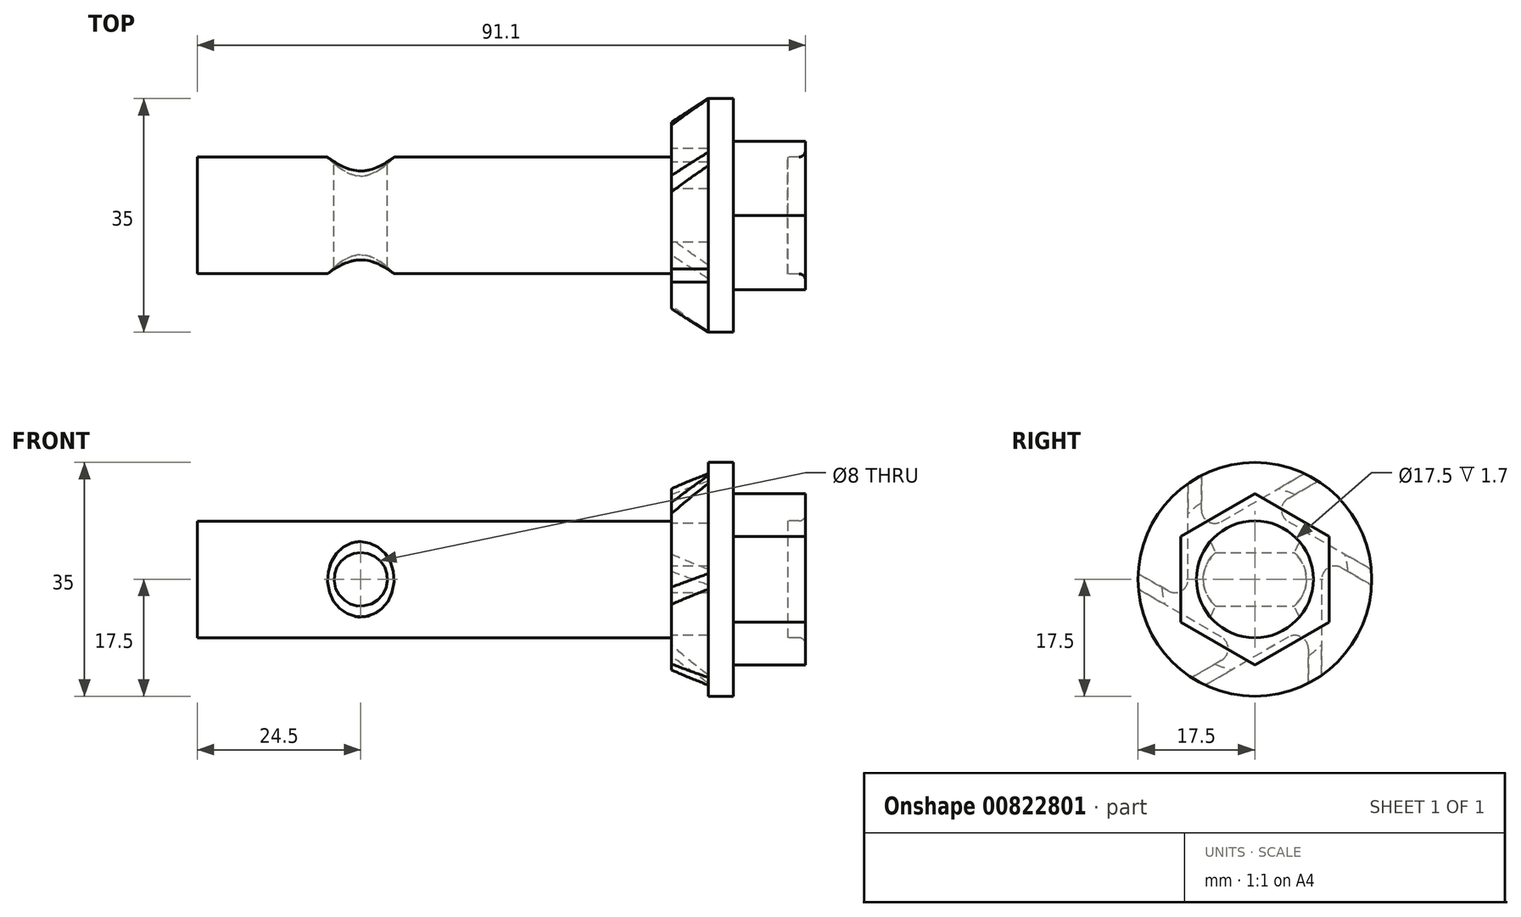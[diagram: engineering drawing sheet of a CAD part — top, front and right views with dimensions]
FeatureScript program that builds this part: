
annotation { "Feature Type Name" : "Feature", "Feature Type Description" : "" }
export const myFeature = defineFeature(function(context is Context, id is Id, definition is map)
    precondition{}
    {
        {
            var Q0;
            Q0=qCreatedBy(makeId("Front.planeOp"),FACE);
            var sketch = newSketch(context, id + "F0", { "sketchPlane" : qUnion([Q0])});
            skLineSegment(sketch, "E0", {"start": v(0, 0) * mm, "end": v(0, 8.73) * mm, "construction": true});
            skLineSegment(sketch, "E1", {"start": v(0, 8.73) * mm, "end": v(-71, 8.73) * mm});
            skLineSegment(sketch, "E2", {"start": v(-71, 8.73) * mm, "end": v(-71, 0) * mm});
            skLineSegment(sketch, "E3", {"start": v(-71, 0) * mm, "end": v(0, 0) * mm});
            skLineSegment(sketch, "E4", {"start": v(0, 8.73) * mm, "end": v(0, 14) * mm});
            skLineSegment(sketch, "E5", {"start": v(5.55, 17.5) * mm, "end": v(9.3, 17.5) * mm});
            skLineSegment(sketch, "E6", {"start": v(9.3, 17.5) * mm, "end": v(9.3, 14) * mm});
            skLineSegment(sketch, "E7", {"start": v(9.3, 14) * mm, "end": v(20.1, 14) * mm});
            skLineSegment(sketch, "E8", {"start": v(20.1, 14) * mm, "end": v(20.1, 8.75) * mm});
            skLineSegment(sketch, "E9", {"start": v(17.4, 0) * mm, "end": v(0, 0) * mm});
            skLineSegment(sketch, "E10", {"start": v(17.4, 0) * mm, "end": v(17.4, 8.75) * mm});
            skLineSegment(sketch, "E11", {"start": v(17.4, 8.75) * mm, "end": v(20.1, 8.75) * mm});
            skPoint(sketch, "E12.orphan", {"position": v(20.1, 0) * mm});
            skLineSegment(sketch, "E13", {"start": v(5.55, 17.5) * mm, "end": v(0, 14) * mm});
            skSolve(sketch);
        }
        {
            var Q0;
            Q0=qSketchRegion(id+"F0",true);
            var Q1;
            Q1=sQuery(id+"F0.wireOp",EDGE,"E3");
            revolve(context, id + "F1", {"surfaceOperationType" : NewSurfaceOperationType.NEW, "entities" : qUnion([Q0]), "axis" : qUnion([Q1]), "revolveType" : RevolveType.FULL});
        }
        {
            var Q0;
            Q0=makeQuery(id+"F1.opRevolve","SWEPT_FACE",FACE,{"disambiguationData":[OSD([sQuery(id+"F0.wireOp",EDGE,"E8")])]});
            var sketch = newSketch(context, id + "F2", { "sketchPlane" : qUnion([Q0])});
            skCircle(sketch, "E14.cCircle", {"center": v(0, 0) * mm, "radius": 11.11 * mm, "construction": true});
            skLineSegment(sketch, "E14.0", {"start": v(-11.11, -6.42) * mm, "end": v(-11.11, 6.42) * mm});
            skLineSegment(sketch, "E14.1", {"start": v(-11.11, 6.42) * mm, "end": v(0, 12.83) * mm});
            skLineSegment(sketch, "E14.2", {"start": v(0, 12.83) * mm, "end": v(11.11, 6.42) * mm});
            skLineSegment(sketch, "E14.3", {"start": v(11.11, 6.42) * mm, "end": v(11.11, -6.42) * mm});
            skLineSegment(sketch, "E14.4", {"start": v(11.11, -6.42) * mm, "end": v(0, -12.83) * mm});
            skLineSegment(sketch, "E14.5", {"start": v(0, -12.83) * mm, "end": v(-11.11, -6.42) * mm});
            skPoint(sketch, "E14.0.midPoint", {"position": v(-11.11, 0) * mm});
            skCircle(sketch, "E15", {"center": v(0, 0) * mm, "radius": 15.48 * mm});
            skSolve(sketch);
        }
        {
            var Q0;
            Q0=qSketchRegion(id+"F2",true);
            var Q1;
            Q1=makeQuery(id+"F1.opRevolve","SWEPT_FACE",FACE,{"disambiguationData":[OSD([sQuery(id+"F0.wireOp",EDGE,"E6")])]});
            extrude(context, id + "F3", {"entities" : qUnion([Q0]), "operationType" : NewBodyOperationType.REMOVE, "endBound" : BoundingType.UP_TO_SURFACE, "oppositeDirection" : true, "depth" : 25 * mm, "endBoundEntityFace" : qUnion([Q1]), "offsetDistance" : 25 * mm});
        }
        {
            var Q0;
            Q0=makeQuery(id+"F1.opRevolve","SWEPT_EDGE",EDGE,{"disambiguationData":[OSD([sQuery(id+"F0.wireOp",EDGE,"E8"),sQuery(id+"F0.wireOp",EDGE,"E11")])]});
            fillet(context, id + "F4", {"entities" : qUnion([Q0]), "radius" : 1 * mm, "tangentPropagation" : true, "allowEdgeOverflow" : false});
        }
        {
            var Q0;
            Q0=makeQuery(id+"F1.opRevolve","SWEPT_FACE",FACE,{"disambiguationData":[OSD([sQuery(id+"F0.wireOp",EDGE,"E4")])]});
            var sketch = newSketch(context, id + "F5", { "sketchPlane" : qUnion([Q0])});
            skCircle(sketch, "E16.0", {"center": v(0, 0) * mm, "radius": 17.5 * mm, "construction": true});
            skLineSegment(sketch, "E17.1.0", {"start": v(-0.3, -17.5) * mm, "end": v(-0.3, -17.5) * mm});
            skLineSegment(sketch, "E18", {"start": v(17.5, 0) * mm, "end": v(14, 0) * mm, "construction": true});
            skLineSegment(sketch, "E19", {"start": v(14, 0) * mm, "end": v(10, 0) * mm, "construction": true});
            skArc(sketch, "E20", {"start": v(10, 0) * mm, "mid": v(11, -1.73) * mm, "end": v(13, -1.73) * mm});
            skLineSegment(sketch, "E21", {"start": v(10, 0) * mm, "end": v(10, 18.81) * mm});
            skLineSegment(sketch, "E22", {"start": v(13, -1.73) * mm, "end": v(23.88, 4.55) * mm});
            skLineSegment(sketch, "E23", {"start": v(10, 18.81) * mm, "end": v(23.88, 4.55) * mm});
            skLineSegment(sketch, "E24.1.0", {"start": v(-11.3, 18.07) * mm, "end": v(8, 22.95) * mm});
            skArc(sketch, "E24.1.1", {"start": v(5, 8.66) * mm, "mid": v(7, 8.66) * mm, "end": v(8, 10.4) * mm});
            skLineSegment(sketch, "E24.1.2", {"start": v(5, 8.66) * mm, "end": v(-11.3, 18.07) * mm});
            skLineSegment(sketch, "E24.1.3", {"start": v(8, 10.4) * mm, "end": v(8, 22.95) * mm});
            skLineSegment(sketch, "E24.1.4", {"start": v(8.75, 15.16) * mm, "end": v(7, 12.12) * mm, "construction": true});
            skLineSegment(sketch, "E24.1.5", {"start": v(7, 12.12) * mm, "end": v(5, 8.66) * mm, "construction": true});
            skLineSegment(sketch, "E24.2.0", {"start": v(-21.3, -0.74) * mm, "end": v(-15.88, 18.4) * mm});
            skArc(sketch, "E24.2.1", {"start": v(-5, 8.66) * mm, "mid": v(-4, 10.4) * mm, "end": v(-5, 12.12) * mm});
            skLineSegment(sketch, "E24.2.2", {"start": v(-5, 8.66) * mm, "end": v(-21.3, -0.74) * mm});
            skLineSegment(sketch, "E24.2.3", {"start": v(-5, 12.12) * mm, "end": v(-15.88, 18.4) * mm});
            skLineSegment(sketch, "E24.2.4", {"start": v(-8.75, 15.16) * mm, "end": v(-7, 12.12) * mm, "construction": true});
            skLineSegment(sketch, "E24.2.5", {"start": v(-7, 12.12) * mm, "end": v(-5, 8.66) * mm, "construction": true});
            skLineSegment(sketch, "E24.3.0", {"start": v(-10, -18.81) * mm, "end": v(-23.88, -4.55) * mm});
            skArc(sketch, "E24.3.1", {"start": v(-10, 0) * mm, "mid": v(-11, 1.73) * mm, "end": v(-13, 1.73) * mm});
            skLineSegment(sketch, "E24.3.2", {"start": v(-10, 0) * mm, "end": v(-10, -18.81) * mm});
            skLineSegment(sketch, "E24.3.3", {"start": v(-13, 1.73) * mm, "end": v(-23.88, -4.55) * mm});
            skLineSegment(sketch, "E24.3.4", {"start": v(-17.5, 0) * mm, "end": v(-14, 0) * mm, "construction": true});
            skLineSegment(sketch, "E24.3.5", {"start": v(-14, 0) * mm, "end": v(-10, 0) * mm, "construction": true});
            skLineSegment(sketch, "E24.4.0", {"start": v(11.3, -18.07) * mm, "end": v(-8, -22.95) * mm});
            skArc(sketch, "E24.4.1", {"start": v(-5, -8.66) * mm, "mid": v(-7, -8.66) * mm, "end": v(-8, -10.4) * mm});
            skLineSegment(sketch, "E24.4.2", {"start": v(-5, -8.66) * mm, "end": v(11.3, -18.07) * mm});
            skLineSegment(sketch, "E24.4.3", {"start": v(-8, -10.4) * mm, "end": v(-8, -22.95) * mm});
            skLineSegment(sketch, "E24.4.4", {"start": v(-8.75, -15.16) * mm, "end": v(-7, -12.12) * mm, "construction": true});
            skLineSegment(sketch, "E24.4.5", {"start": v(-7, -12.12) * mm, "end": v(-5, -8.66) * mm, "construction": true});
            skLineSegment(sketch, "E24.5.0", {"start": v(21.3, 0.74) * mm, "end": v(15.88, -18.4) * mm});
            skArc(sketch, "E24.5.1", {"start": v(5, -8.66) * mm, "mid": v(4, -10.4) * mm, "end": v(5, -12.12) * mm});
            skLineSegment(sketch, "E24.5.2", {"start": v(5, -8.66) * mm, "end": v(21.3, 0.74) * mm});
            skLineSegment(sketch, "E24.5.3", {"start": v(5, -12.12) * mm, "end": v(15.88, -18.4) * mm});
            skLineSegment(sketch, "E24.5.4", {"start": v(8.75, -15.16) * mm, "end": v(7, -12.12) * mm, "construction": true});
            skLineSegment(sketch, "E24.5.5", {"start": v(7, -12.12) * mm, "end": v(5, -8.66) * mm, "construction": true});
            skSolve(sketch);
        }
        {
            var Q0;
            Q0=qSketchRegion(id+"F5",true);
            extrude(context, id + "F6", {"entities" : qUnion([Q0]), "operationType" : NewBodyOperationType.REMOVE, "oppositeDirection" : true, "depth" : 5.55 * mm, "offsetDistance" : 25 * mm});
        }
        {
            var Q0;
            Q0=qCreatedBy(makeId("Front.planeOp"),FACE);
            var sketch = newSketch(context, id + "F7", { "sketchPlane" : qUnion([Q0])});
            skLineSegment(sketch, "E25", {"start": v(0, 0) * mm, "end": v(-46.5, 0) * mm, "construction": true});
            skCircle(sketch, "E26", {"center": v(-46.5, 0) * mm, "radius": 4 * mm});
            skSolve(sketch);
        }
        {
            var Q0;
            Q0=qSketchRegion(id+"F7",true);
            extrude(context, id + "F8", {"entities" : qUnion([Q0]), "operationType" : NewBodyOperationType.REMOVE, "endBound" : BoundingType.SYMMETRIC, "depth" : 25 * mm, "offsetDistance" : 25 * mm});
        }
        {
            var Q0;
            Q0=makeQuery(id+"F8.boolean.opBoolean","COPY",FACE,{"derivedFrom":makeQuery(id+"F8.opExtrude","SWEPT_FACE",FACE,{"disambiguationData":[OSD([sQuery(id+"F7.wireOp",EDGE,"E26")])]})});
            chamfer(context, id + "F9", {"entities" : qUnion([Q0]), "width" : 1 * mm, "tangentPropagation" : true});
        }
    });
